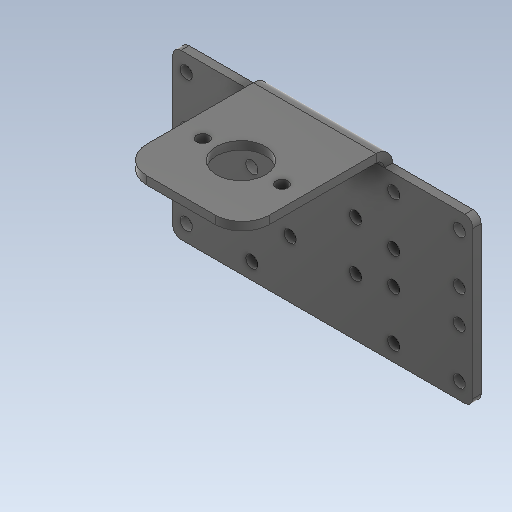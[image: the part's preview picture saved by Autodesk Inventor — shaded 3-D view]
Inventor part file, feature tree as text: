
AUTODESK INVENTOR PART (.ipt)
format: ipt  version: 2020 (Build 240168000, 168)  size: 230,912 bytes
history: native  units: mm
features: sheet_metal_op x6, sketch x6, other x6, fillet x2, pattern_linear x1, mirror x1
ambient origin geometry x8: Origin, YZ Plane, XZ Plane, XY Plane, X Axis, Y Axis, Z Axis, Center Point
bodies: Solid1 (feature_tree)
feature tree (22):
  sheet_metal_op  "Face1"
  pattern_linear  "Rectangular Pattern1"  Count1=11  [1 undecoded]
  mirror  "Mirror1"
  sheet_metal_op  "Face2"
  sheet_metal_op  "Flange1"
  fillet  "Fillet2"  Radius=60.0mm
  fillet  "Fillet4"  Radius=3.0mm
  sketch  "Sketch1"  dims[d4=24.0mm d5=18.0mm d8=4.5mm d9=4.5mm d10=4.5mm d11=4.5mm]
  other  "Plate1"
  sketch  "Sketch2"  dims[d12=5.0mm]
  sketch  "Sketch3"  dims[d13=15.0mm]
  sketch  "Sketch4"  dims[d14=3.0mm]
  other  "Plate2"
  sheet_metal_op  "Bend1"
  sketch  "Sketch5"  dims[d15=0.0mm]
  other  "Plate3"
  sheet_metal_op  "Bend2"
  sheet_metal_op  "Corner1"
  sketch  "Sketch6"  dims[d16=20.0mm d18=30.0mm d20=24.0mm d21=18.0mm d22=4.5mm d23=4.5mm d24=4.5mm d25=4.5mm d26=12.0mm d27=9.0mm d28=3.0mm d29=0.0mm d30=45.0mm d31=3.0mm d32=22.5mm d33=3.0mm d34=3.0mm d35=1.5mm d36=6.0mm d37=3.0mm d38=3.0mm d39=1.5mm d40=6.0mm d41=3.0mm d42=55.0mm d43=90.0deg d44=3.0mm d45=12.0mm d46=3.0mm d47=3.0mm d48=18.0mm d49=33.0mm d50=4.5mm d51=4.5mm d52=29.0mm d53=22.5mm d54=15.0mm d55=33.0mm d56=33.0mm d57=3.0mm d58=0.0mm d59=10.0mm d60=0.0mm d102=3.0mm]
  other  "Cut1"
  other  "Cut2"
  other  "Cut3"
note: 1 required parameter value undecoded (feature->parameter linkage not recoverable at this tier; creation-order binding heuristic only, values carry confidence <= 0.55)
